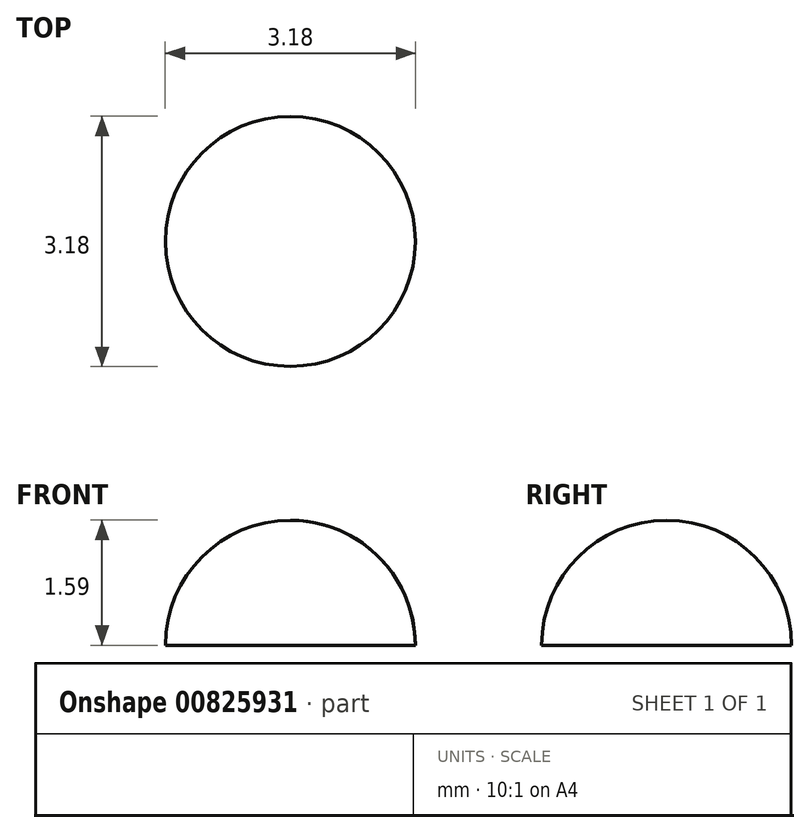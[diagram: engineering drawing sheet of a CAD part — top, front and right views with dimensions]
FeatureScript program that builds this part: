
annotation { "Feature Type Name" : "Feature", "Feature Type Description" : "" }
export const myFeature = defineFeature(function(context is Context, id is Id, definition is map)
    precondition{}
    {
        {
            var Q0;
            Q0=qCreatedBy(makeId("Front.planeOp"),FACE);
            var sketch = newSketch(context, id + "F0", { "sketchPlane" : qUnion([Q0])});
            skArc(sketch, "E0", {"start": v(1.59, 0) * mm, "mid": v(1.12, 1.12) * mm, "end": v(0, 1.59) * mm});
            skLineSegment(sketch, "E1", {"start": v(0, 1.59) * mm, "end": v(0, 0) * mm});
            skLineSegment(sketch, "E2", {"start": v(0, 0) * mm, "end": v(1.59, 0) * mm});
            skSolve(sketch);
        }
        {
            var Q0;
            Q0=sQuery(id+"F0.wireOp",EDGE,"E0");
            var Q1;
            Q1=sQuery(id+"F0.wireOp",EDGE,"E2");
            var Q2;
            Q2=sQuery(id+"F0.wireOp",EDGE,"E1");
            revolve(context, id + "F1", {"bodyType" : ToolBodyType.SURFACE, "surfaceOperationType" : NewSurfaceOperationType.NEW, "surfaceEntities" : qUnion([Q0, Q1]), "axis" : qUnion([Q2]), "revolveType" : RevolveType.FULL});
        }
    });
